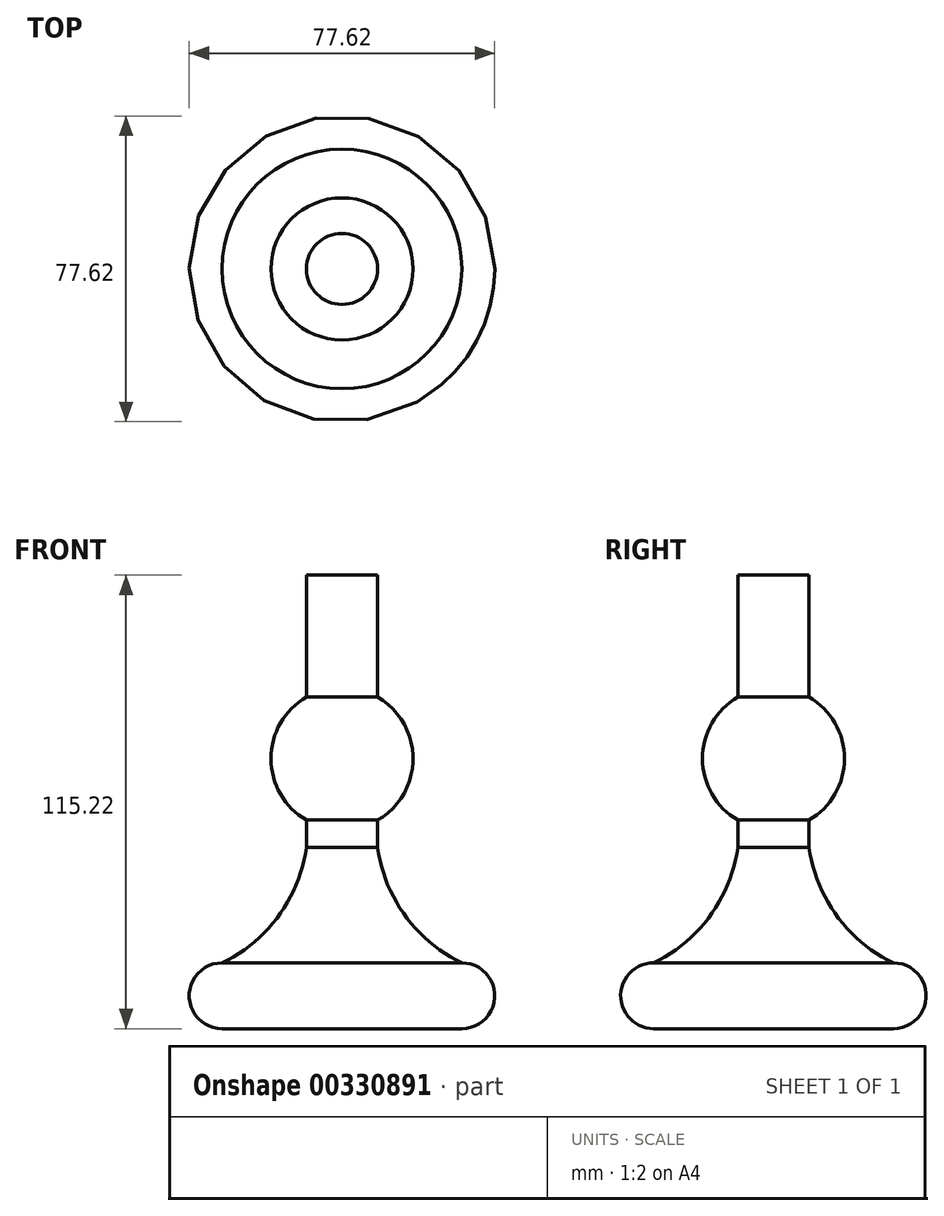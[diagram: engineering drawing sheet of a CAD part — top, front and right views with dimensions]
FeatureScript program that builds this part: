
annotation { "Feature Type Name" : "Feature", "Feature Type Description" : "" }
export const myFeature = defineFeature(function(context is Context, id is Id, definition is map)
    precondition{}
    {
        {
            var Q0;
            Q0=qCreatedBy(makeId("Front.planeOp"),FACE);
            var sketch = newSketch(context, id + "F0", { "sketchPlane" : qUnion([Q0])});
            skLineSegment(sketch, "E0", {"start": v(0, 0) * mm, "end": v(30.45, 0) * mm});
            skArc(sketch, "E1", {"start": v(30.45, 0) * mm, "mid": v(38.81, 8.36) * mm, "end": v(30.45, 16.73) * mm});
            skArc(sketch, "E2", {"start": v(9.02, 46.05) * mm, "mid": v(16.07, 28.7) * mm, "end": v(30.45, 16.73) * mm});
            skLineSegment(sketch, "E3", {"start": v(9.02, 46.05) * mm, "end": v(9.02, 52.97) * mm});
            skLineSegment(sketch, "E4", {"start": v(9.02, 115.22) * mm, "end": v(0, 115.22) * mm});
            skLineSegment(sketch, "E5", {"start": v(0, 115.22) * mm, "end": v(0, 0) * mm});
            skArc(sketch, "E6", {"start": v(9.02, 52.97) * mm, "mid": v(18.05, 68.6) * mm, "end": v(9.02, 84.24) * mm});
            skLineSegment(sketch, "E7.trimOffspring", {"start": v(9.02, 84.24) * mm, "end": v(9.02, 115.22) * mm});
            skSolve(sketch);
        }
        {
            var Q0;
            Q0=makeQuery(id+"F0.imprint","IMPRINT",FACE,{"disambiguationData":[TD([[makeQuery(id+"F0.imprint","IMPRINT",EDGE,{"derivedFrom":sQuery(id+"F0.wireOp",EDGE,"E0")}),1.0]])]});
            var Q1;
            Q1=sQuery(id+"F0.wireOp",EDGE,"E5");
            revolve(context, id + "F1", {"entities" : qUnion([Q0]), "axis" : qUnion([Q1]), "revolveType" : RevolveType.FULL});
        }
    });
